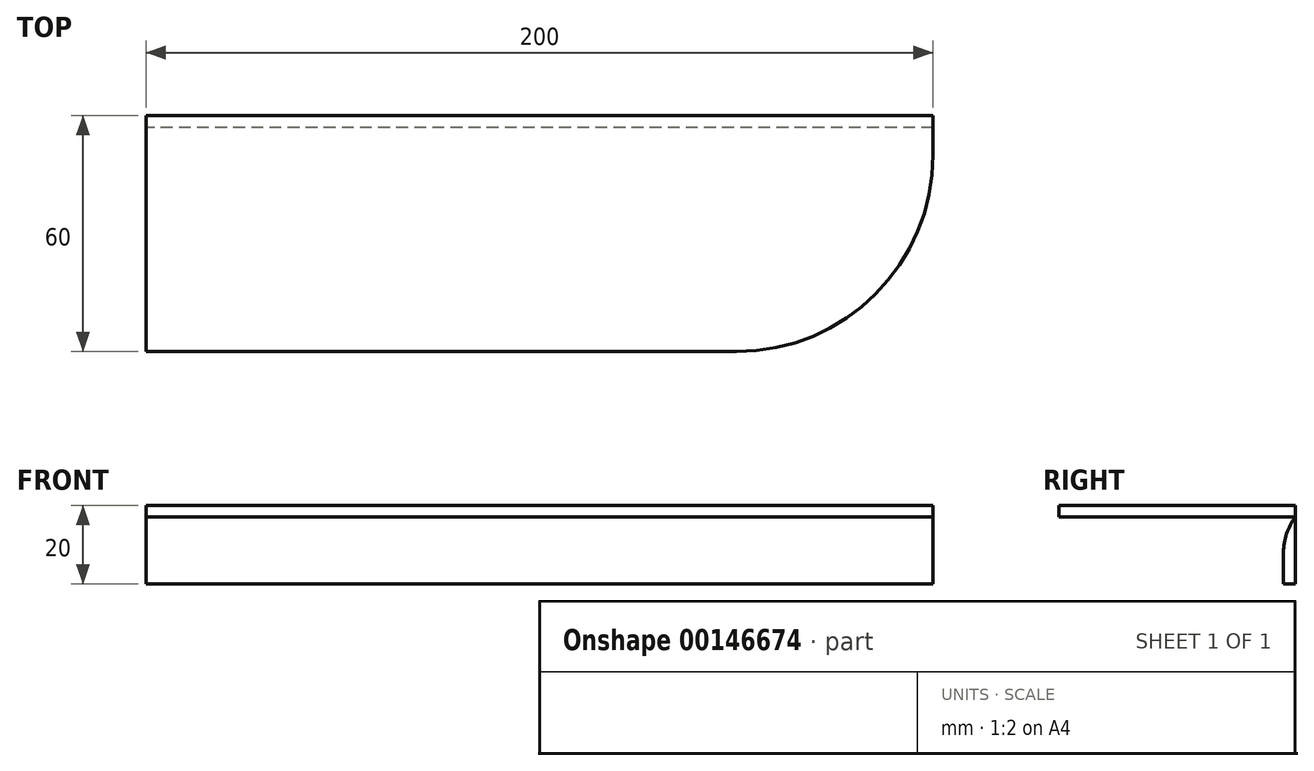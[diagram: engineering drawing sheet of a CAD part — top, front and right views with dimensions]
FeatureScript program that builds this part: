
annotation { "Feature Type Name" : "Feature", "Feature Type Description" : "" }
export const myFeature = defineFeature(function(context is Context, id is Id, definition is map)
    precondition{}
    {
        {
            var Q0;
            Q0=qCreatedBy(makeId("Top.planeOp"),FACE);
            var sketch = newSketch(context, id + "F0", { "sketchPlane" : qUnion([Q0])});
            skLineSegment(sketch, "E0.bottom", {"start": v(-108.98, -5.03) * mm, "end": v(91.02, -5.03) * mm});
            skLineSegment(sketch, "E0.top", {"start": v(-108.98, -65.03) * mm, "end": v(41.02, -65.03) * mm});
            skLineSegment(sketch, "E0.left", {"start": v(-108.98, -5.03) * mm, "end": v(-108.98, -65.03) * mm});
            skLineSegment(sketch, "E0.right", {"start": v(91.02, -5.03) * mm, "end": v(91.02, -15.03) * mm});
            skPoint(sketch, "E1.visualSharp", {"position": v(91.02, -65.03) * mm});
            skArc(sketch, "E1.filletArc", {"start": v(41.02, -65.03) * mm, "mid": v(76.37, -50.38) * mm, "end": v(91.02, -15.03) * mm});
            skSolve(sketch);
        }
        {
            var Q0;
            Q0=makeQuery(id+"F0.imprint","IMPRINT",FACE,{"disambiguationData":[TD([[makeQuery(id+"F0.imprint","IMPRINT",EDGE,{"derivedFrom":sQuery(id+"F0.wireOp",EDGE,"E0.bottom")}),-1.0]])]});
            extrude(context, id + "F1", {"entities" : qUnion([Q0]), "depth" : 3 * mm});
        }
        {
            var Q0;
            Q0=makeQuery(id+"F1.opExtrude","SWEPT_FACE",FACE,{"disambiguationData":[OSD([sQuery(id+"F0.wireOp",EDGE,"E0.bottom")])]});
            var sketch = newSketch(context, id + "F2", { "sketchPlane" : qUnion([Q0])});
            skLineSegment(sketch, "E2.bottom", {"start": v(-91.02, 0) * mm, "end": v(108.98, 0) * mm});
            skLineSegment(sketch, "E2.top", {"start": v(-91.02, -17) * mm, "end": v(108.98, -17) * mm});
            skLineSegment(sketch, "E2.left", {"start": v(-91.02, 0) * mm, "end": v(-91.02, -17) * mm});
            skLineSegment(sketch, "E2.right", {"start": v(108.98, 0) * mm, "end": v(108.98, -17) * mm});
            skSolve(sketch);
        }
        {
            var Q0;
            Q0=makeQuery(id+"F2.imprint","IMPRINT",FACE,{"disambiguationData":[TD([[makeQuery(id+"F2.imprint","IMPRINT",EDGE,{"derivedFrom":sQuery(id+"F2.wireOp",EDGE,"E2.bottom")}),1.0]])]});
            extrude(context, id + "F3", {"entities" : qUnion([Q0]), "oppositeDirection" : true, "depth" : 3 * mm});
        }
        {
            var Q0;
            Q0=makeQuery(id+"F3.opExtrude","CAP_EDGE",EDGE,{"disambiguationData":[OSD([sQuery(id+"F2.wireOp",EDGE,"E2.bottom")])],"isStart":false});
            fillet(context, id + "F4", {"entities" : qUnion([Q0]), "radius" : 15 * mm, "tangentPropagation" : true, "allowEdgeOverflow" : false});
        }
    });
